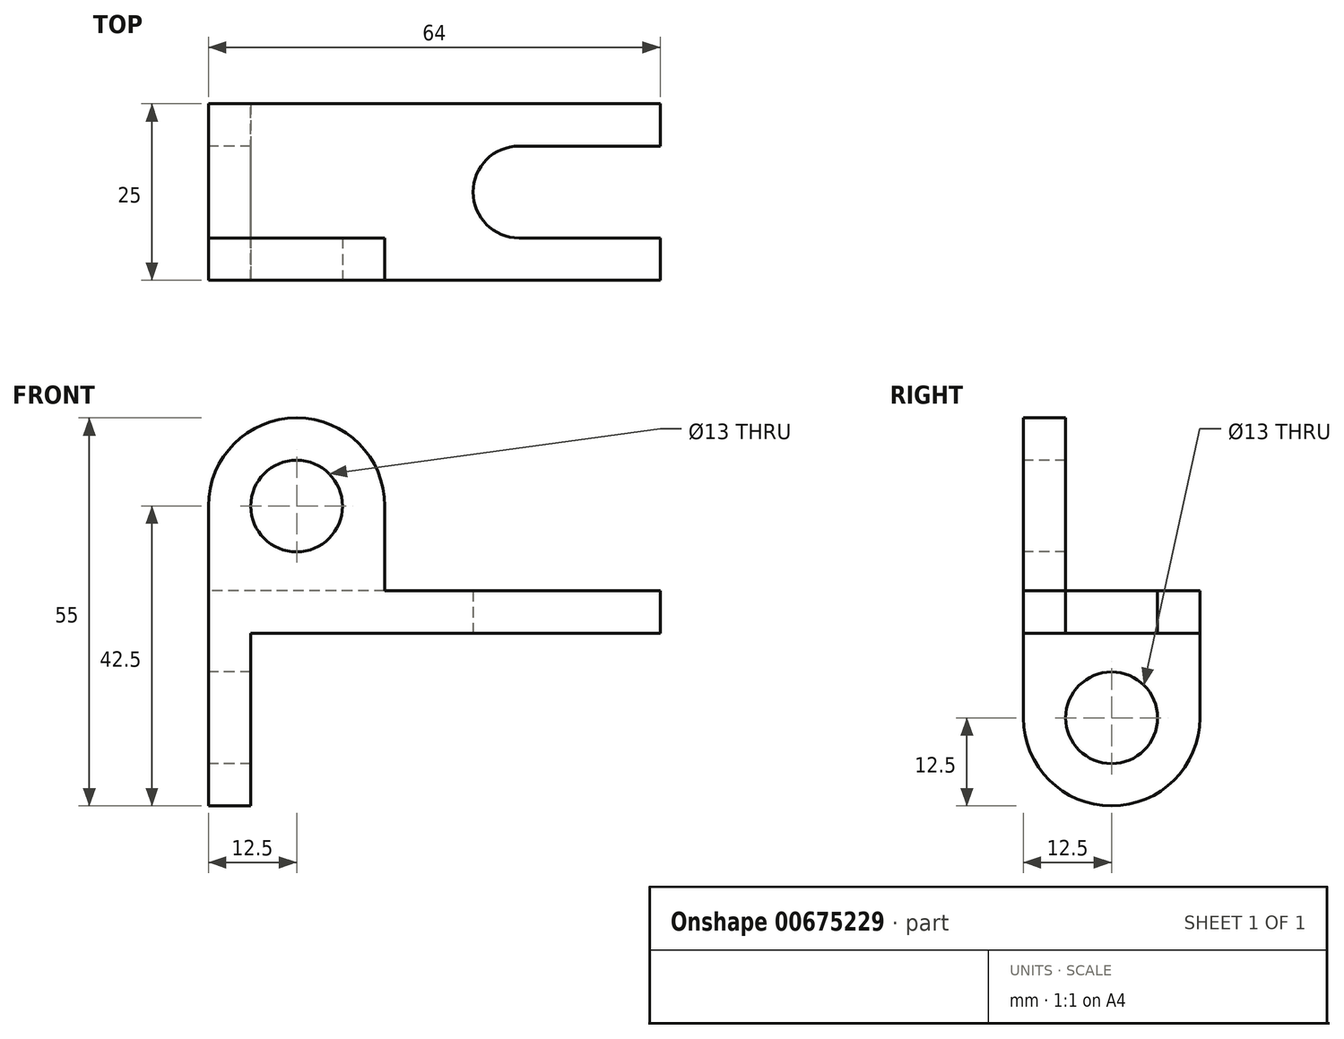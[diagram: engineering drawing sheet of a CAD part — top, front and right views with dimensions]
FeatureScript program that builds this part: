
annotation { "Feature Type Name" : "Feature", "Feature Type Description" : "" }
export const myFeature = defineFeature(function(context is Context, id is Id, definition is map)
    precondition{}
    {
        {
            var Q0;
            Q0=qCreatedBy(makeId("Top.planeOp"),FACE);
            var sketch = newSketch(context, id + "F0", { "sketchPlane" : qUnion([Q0])});
            skLineSegment(sketch, "E0.bottom", {"start": v(32, -12.5) * mm, "end": v(-32, -12.5) * mm});
            skLineSegment(sketch, "E0.top", {"start": v(32, 12.5) * mm, "end": v(-32, 12.5) * mm});
            skLineSegment(sketch, "E0.left", {"start": v(32, -12.5) * mm, "end": v(32, 12.5) * mm});
            skLineSegment(sketch, "E0.right", {"start": v(-32, -12.5) * mm, "end": v(-32, 12.5) * mm});
            skPoint(sketch, "E0.middle", {"position": v(0, 0) * mm});
            skLineSegment(sketch, "E1.bottom", {"start": v(32, -6.5) * mm, "end": v(12, -6.5) * mm});
            skLineSegment(sketch, "E1.top", {"start": v(32, 6.5) * mm, "end": v(12, 6.5) * mm});
            skLineSegment(sketch, "E1.left", {"start": v(32, -6.5) * mm, "end": v(32, 6.5) * mm});
            skLineSegment(sketch, "E1.right", {"start": v(12, -6.5) * mm, "end": v(12, 6.5) * mm});
            skPoint(sketch, "E1.middle", {"position": v(22, 0) * mm});
            skCircle(sketch, "E2", {"center": v(12, 0) * mm, "radius": 6.5 * mm});
            skSolve(sketch);
        }
        {
            var Q0;
            {var subQ4=sQuery(id+"F0.wireOp",EDGE,"E0.bottom");Q0=makeQuery(id+"F0.imprint","IMPRINT",FACE,{"disambiguationData":[TD([[makeQuery(id+"F0.imprint","IMPRINT",EDGE,{"derivedFrom":subQ4}),-1.0]])]});}
            extrude(context, id + "F1", {"entities" : qUnion([Q0]), "depth" : 6 * mm, "offsetDistance" : 25 * mm});
        }
        {
            var Q0;
            Q0=makeQuery(id+"F1.opExtrude","SWEPT_FACE",FACE,{"disambiguationData":[OSD([sQuery(id+"F0.wireOp",EDGE,"E0.right")])]});
            var sketch = newSketch(context, id + "F2", { "sketchPlane" : qUnion([Q0])});
            skPoint(sketch, "E3.oppositeSnap0", {"position": v(-12.5, 3) * mm});
            skLineSegment(sketch, "E3.bottom", {"start": v(12.5, 6) * mm, "end": v(-12.5, 6) * mm});
            skLineSegment(sketch, "E3.top", {"start": v(12.5, -12) * mm, "end": v(6.5, -12) * mm});
            skLineSegment(sketch, "E3.left", {"start": v(12.5, 6) * mm, "end": v(12.5, -12) * mm});
            skLineSegment(sketch, "E3.right", {"start": v(-12.5, 6) * mm, "end": v(-12.5, -12) * mm});
            skCircle(sketch, "E4", {"center": v(0, -12) * mm, "radius": 12.5 * mm});
            skCircle(sketch, "E5", {"center": v(0, -12) * mm, "radius": 6.5 * mm});
            skLineSegment(sketch, "E6.trimOffspring", {"start": v(-6.5, -12) * mm, "end": v(-12.5, -12) * mm});
            skSolve(sketch);
        }
        {
            var Q0;
            {var subQ0=sQuery(id+"F2.wireOp",EDGE,"E3.top");Q0=makeQuery(id+"F2.imprint","IMPRINT",FACE,{"disambiguationData":[TD([[makeQuery(id+"F2.imprint","IMPRINT",EDGE,{"derivedFrom":subQ0}),1.0]])]});}
            var Q1;
            {var subQ1=sQuery(id+"F2.wireOp",EDGE,"E3.top");Q1=makeQuery(id+"F2.imprint","IMPRINT",FACE,{"disambiguationData":[TD([[makeQuery(id+"F2.imprint","IMPRINT",EDGE,{"derivedFrom":subQ1}),-1.0]])]});}
            var Q2;
            {var subQ0=sQuery(id+"F2.wireOp",EDGE,"E3.left");var subQ1=makeQuery(id+"F1.opExtrude","CAP_EDGE",EDGE,{"disambiguationData":[OSD([sQuery(id+"F0.wireOp",EDGE,"E0.right")])],"isStart":true});var subQ2=makeQuery(id+"F2.imprint","INTERSECT",VERTEX,{"derivedFrom":[subQ1,subQ0]});Q2=makeQuery(id+"F2.imprint","IMPRINT",FACE,{"disambiguationData":[TD([[makeQuery(id+"F2.imprint","IMPRINT",EDGE,{"disambiguationData":[TD([[subQ2,-1.0]])],"derivedFrom":subQ1}),1.0]])]});}
            var Q3;
            {var subQ0=sQuery(id+"F2.wireOp",EDGE,"E3.right");var subQ1=makeQuery(id+"F1.opExtrude","CAP_EDGE",EDGE,{"disambiguationData":[OSD([sQuery(id+"F0.wireOp",EDGE,"E0.right")])],"isStart":true});var subQ2=makeQuery(id+"F2.imprint","INTERSECT",VERTEX,{"derivedFrom":[subQ1,subQ0]});Q3=makeQuery(id+"F2.imprint","IMPRINT",FACE,{"disambiguationData":[TD([[makeQuery(id+"F2.imprint","IMPRINT",EDGE,{"disambiguationData":[TD([[subQ2,1.0]])],"derivedFrom":subQ1}),1.0]])]});}
            extrude(context, id + "F3", {"entities" : qUnion([Q0, Q1, Q2, Q3]), "operationType" : NewBodyOperationType.ADD, "oppositeDirection" : true, "depth" : 6 * mm, "offsetDistance" : 25 * mm});
        }
        {
            var Q0;
            Q0=makeQuery(id+"F3.boolean.opBoolean","MERGE",FACE,{"derivedFrom":[makeQuery(id+"F1.opExtrude","SWEPT_FACE",FACE,{"disambiguationData":[OSD([sQuery(id+"F0.wireOp",EDGE,"E0.bottom")])]}),makeQuery(id+"F3.opExtrude","SWEPT_FACE",FACE,{"disambiguationData":[OSD([sQuery(id+"F2.wireOp",EDGE,"E3.left")])]})]});
            var sketch = newSketch(context, id + "F4", { "sketchPlane" : qUnion([Q0])});
            skLineSegment(sketch, "E7.bottom", {"start": v(-32, 0) * mm, "end": v(-7, 0) * mm});
            skLineSegment(sketch, "E7.top", {"start": v(-32, 18) * mm, "end": v(-7, 18) * mm});
            skLineSegment(sketch, "E7.left", {"start": v(-32, 0) * mm, "end": v(-32, 18) * mm});
            skLineSegment(sketch, "E7.right", {"start": v(-7, 0) * mm, "end": v(-7, 18) * mm});
            skArc(sketch, "E8", {"start": v(-7, 18) * mm, "mid": v(-19.5, 30.5) * mm, "end": v(-32, 18) * mm});
            skSolve(sketch);
        }
        {
            var Q0;
            {var subQ0=sQuery(id+"F4.wireOp",EDGE,"E7.top");Q0=makeQuery(id+"F4.imprint","IMPRINT",FACE,{"disambiguationData":[TD([[makeQuery(id+"F4.imprint","IMPRINT",EDGE,{"derivedFrom":subQ0}),-1.0]])]});}
            var Q1;
            Q1=makeQuery(id+"F4.imprint","IMPRINT",FACE,{"disambiguationData":[TD([[makeQuery(id+"F4.imprint","IMPRINT",EDGE,{"derivedFrom":sQuery(id+"F4.wireOp",EDGE,"E7.top")}),1.0]])]});
            extrude(context, id + "F5", {"entities" : qUnion([Q0, Q1]), "operationType" : NewBodyOperationType.ADD, "oppositeDirection" : true, "depth" : 6 * mm, "offsetDistance" : 25 * mm});
        }
        {
            var Q0;
            Q0=sQuery(id+"F4.wireOp",VERTEX,"E8.center");
            var Q1;
            Q1=makeQuery(id+"F1.opExtrude","SWEPT_BODY",BODY,{"disambiguationData":[OSD([sQuery(id+"F0.wireOp",EDGE,"E0.bottom"),sQuery(id+"F0.wireOp",EDGE,"E0.top"),sQuery(id+"F0.wireOp",EDGE,"E0.left"),sQuery(id+"F0.wireOp",EDGE,"E0.right"),sQuery(id+"F0.wireOp",EDGE,"E1.bottom"),sQuery(id+"F0.wireOp",EDGE,"E1.top"),sQuery(id+"F0.wireOp",EDGE,"E1.right"),sQuery(id+"F0.wireOp",EDGE,"E2")])]});
            hole(context, id + "F6", {"style" : HoleStyle.SIMPLE, "endStyle" : HoleEndStyle.THROUGH, "holeDiameter" : 13 * mm, "majorDiameter" : 5 * mm, "isTappedThrough" : true, "tappedDepth" : 12 * mm, "tapClearance" : 3, "locations" : qUnion([Q0]), "scope" : qUnion([Q1])});
        }
    });
